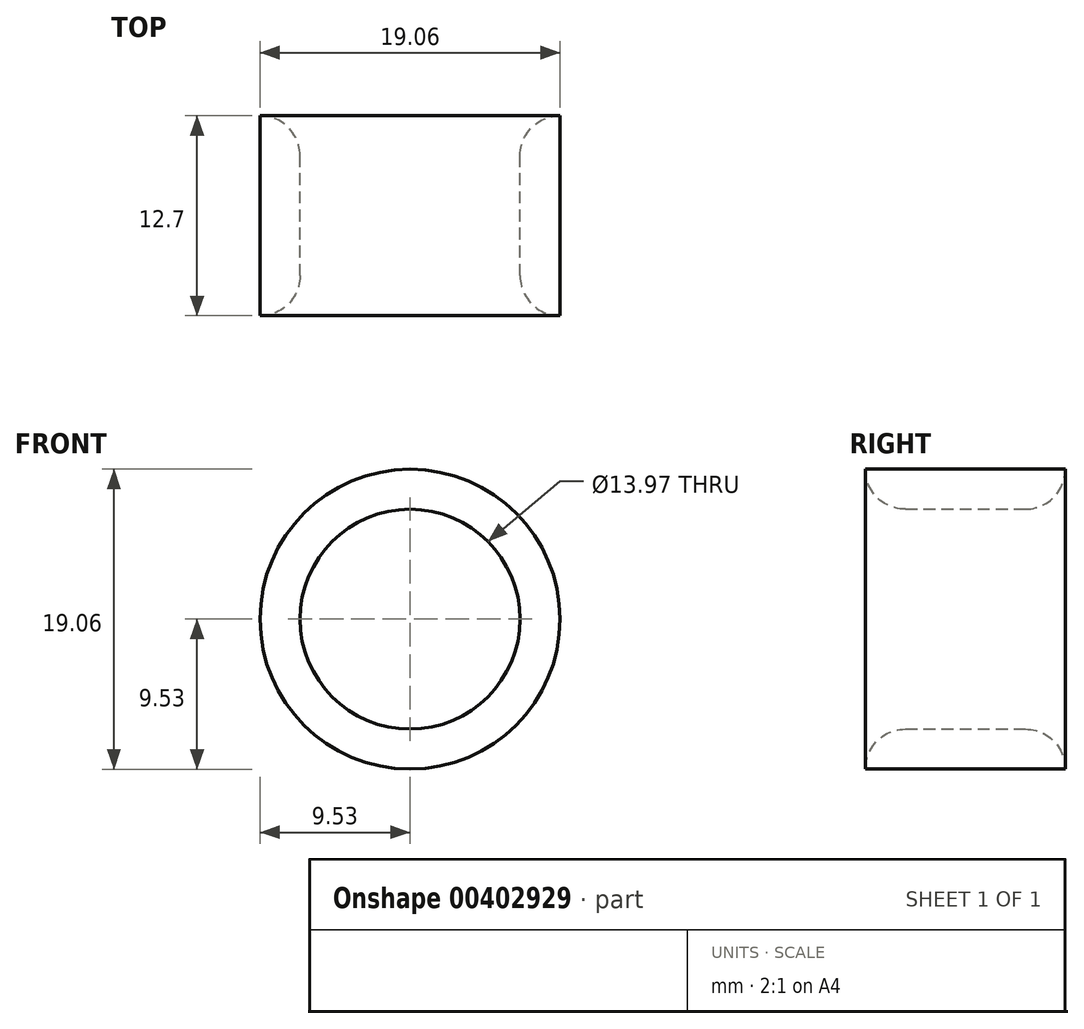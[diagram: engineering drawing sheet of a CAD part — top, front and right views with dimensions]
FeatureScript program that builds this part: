
annotation { "Feature Type Name" : "Feature", "Feature Type Description" : "" }
export const myFeature = defineFeature(function(context is Context, id is Id, definition is map)
    precondition{}
    {
        {
            var Q0;
            Q0=qCreatedBy(makeId("Front.planeOp"),FACE);
            var sketch = newSketch(context, id + "F0", { "sketchPlane" : qUnion([Q0])});
            skCircle(sketch, "E0", {"center": v(0, 0) * mm, "radius": 9.53 * mm});
            skCircle(sketch, "E1", {"center": v(0, 0) * mm, "radius": 6.99 * mm});
            skSolve(sketch);
        }
        {
            var Q0;
            Q0=makeQuery(id+"F0.imprint","IMPRINT",FACE,{"disambiguationData":[TD([[makeQuery(id+"F0.imprint","IMPRINT",EDGE,{"derivedFrom":sQuery(id+"F0.wireOp",EDGE,"E0")}),1.0]])]});
            extrude(context, id + "F1", {"entities" : qUnion([Q0]), "depth" : 12.7 * mm});
        }
        {
            var Q0;
            Q0=makeQuery(id+"F1.opExtrude","CAP_EDGE",EDGE,{"disambiguationData":[OSD([sQuery(id+"F0.wireOp",EDGE,"E1")])],"isStart":false});
            var Q1;
            Q1=makeQuery(id+"F1.opExtrude","CAP_EDGE",EDGE,{"disambiguationData":[OSD([sQuery(id+"F0.wireOp",EDGE,"E1")])],"isStart":true});
            fillet(context, id + "F2", {"entities" : qUnion([Q0, Q1]), "radius" : 2.54 * mm, "tangentPropagation" : true, "allowEdgeOverflow" : false});
        }
        {
            var Q0;
            Q0=qCreatedBy(makeId("Right.planeOp"),FACE);
            cPlane(context, id + "F3", {"entities" : qUnion([Q0]), "cplaneType" : CPlaneType.OFFSET, "offset" : 9.52 * mm, "width" : 152.4 * mm, "height" : 152.4 * mm});
        }
    });
